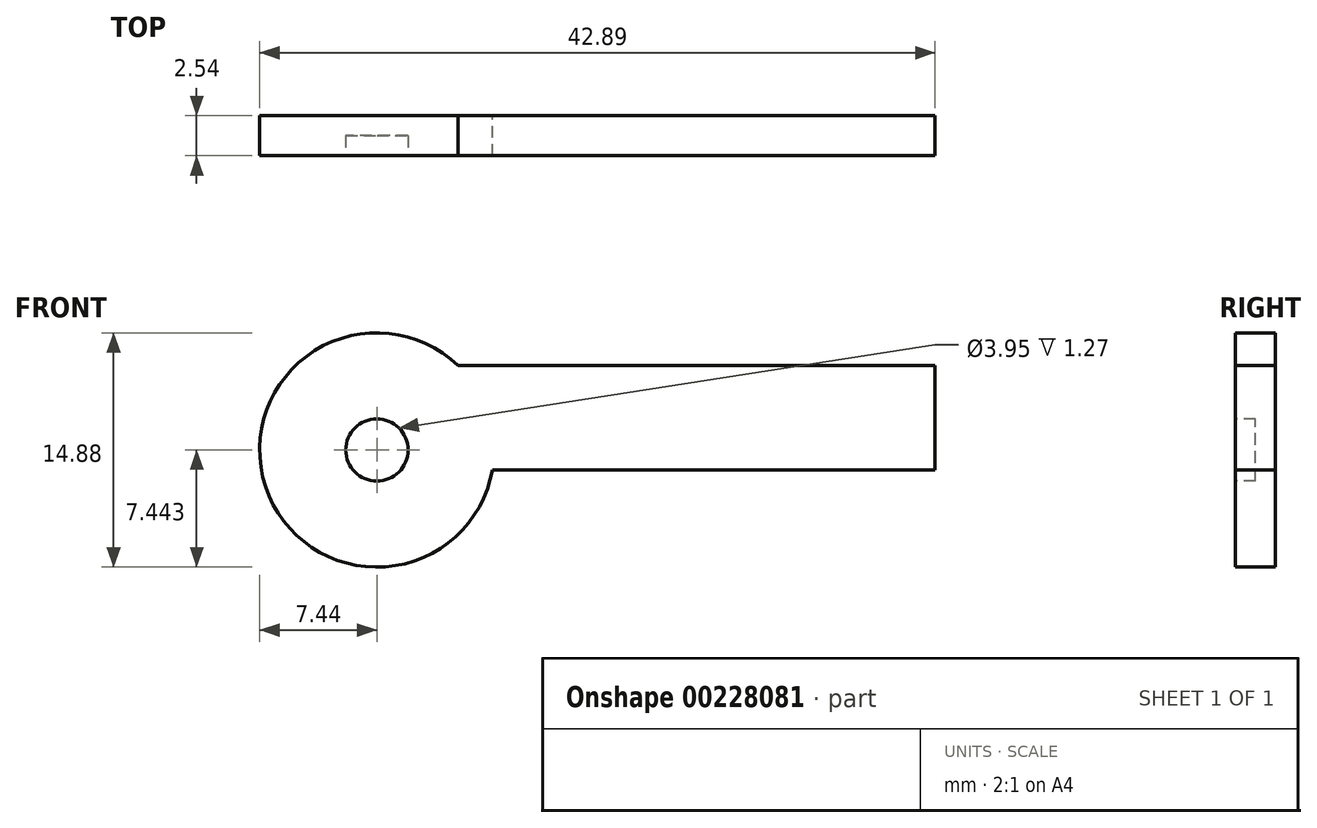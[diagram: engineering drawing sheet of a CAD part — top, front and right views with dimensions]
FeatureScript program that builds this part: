
annotation { "Feature Type Name" : "Feature", "Feature Type Description" : "" }
export const myFeature = defineFeature(function(context is Context, id is Id, definition is map)
    precondition{}
    {
        {
            var Q0;
            Q0=qCreatedBy(makeId("Front.planeOp"),FACE);
            var sketch = newSketch(context, id + "F0", { "sketchPlane" : qUnion([Q0])});
            skCircle(sketch, "E0", {"center": v(-59.85, 55.51) * mm, "radius": 7.44 * mm});
            skLineSegment(sketch, "E1", {"start": v(-54.69, 60.87) * mm, "end": v(-24.4, 60.87) * mm});
            skLineSegment(sketch, "E2", {"start": v(-24.4, 60.87) * mm, "end": v(-24.4, 54.24) * mm});
            skLineSegment(sketch, "E3", {"start": v(-24.4, 54.24) * mm, "end": v(-52.52, 54.24) * mm});
            skSolve(sketch);
        }
        {
            var Q0;
            Q0 = qSketchRegion(id + "F0", true);
            extrude(context, id + "F1", {"entities" : qUnion([Q0]), "depth" : 2.54 * mm});
        }
        {
            var Q0;
            Q0=makeQuery(id+"F1.opExtrude","CAP_FACE",FACE,{"disambiguationData":[OSD([sQuery(id+"F0.wireOp",EDGE,"E0"),sQuery(id+"F0.wireOp",EDGE,"E1"),sQuery(id+"F0.wireOp",EDGE,"E2"),sQuery(id+"F0.wireOp",EDGE,"E3")])],"isStart":false});
            var sketch = newSketch(context, id + "F2", { "sketchPlane" : qUnion([Q0])});
            skCircle(sketch, "E4", {"center": v(-59.85, 55.51) * mm, "radius": 1.98 * mm});
            skSolve(sketch);
        }
        {
            var Q0;
            Q0=makeQuery(id+"F2.imprint","IMPRINT",FACE,{"disambiguationData":[TD([[makeQuery(id+"F2.imprint","IMPRINT",EDGE,{"derivedFrom":sQuery(id+"F2.wireOp",EDGE,"E4")}),1.0]])]});
            var Q1;
            Q1=sQuery(id+"F2.wireOp",EDGE,"E4");
            extrude(context, id + "F3", {"entities" : qUnion([Q0]), "operationType" : NewBodyOperationType.REMOVE, "surfaceEntities" : qUnion([Q1]), "oppositeDirection" : true, "depth" : 1.27 * mm});
        }
    });
